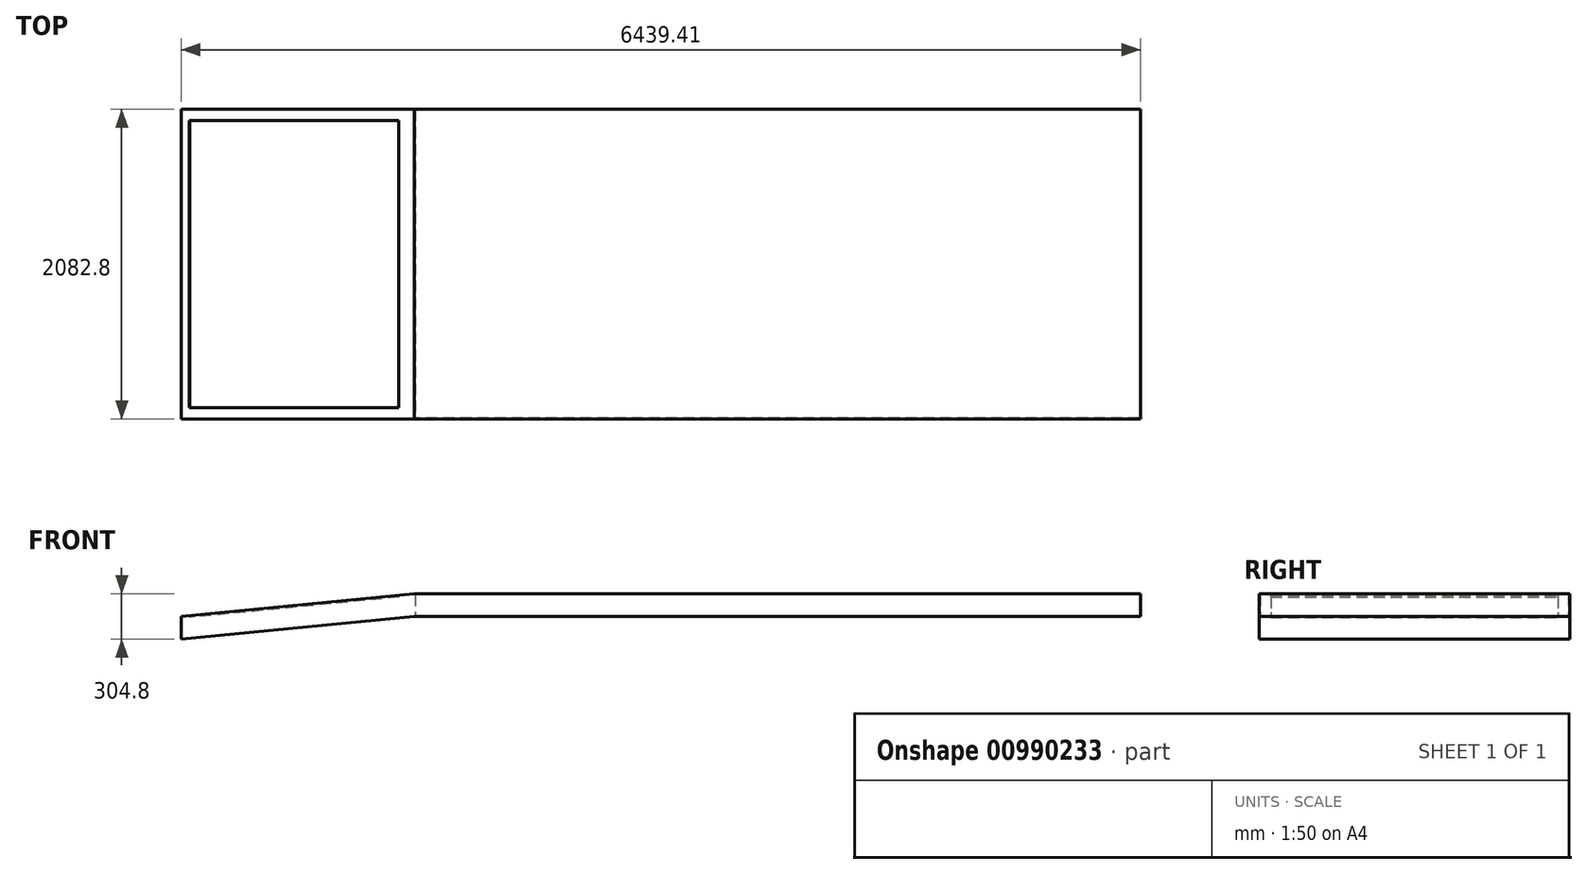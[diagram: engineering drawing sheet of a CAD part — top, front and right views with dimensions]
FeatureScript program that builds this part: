
annotation { "Feature Type Name" : "Feature", "Feature Type Description" : "" }
export const myFeature = defineFeature(function(context is Context, id is Id, definition is map)
    precondition{}
    {
        {
            var Q0;
            Q0=qCreatedBy(makeId("Top.planeOp"),FACE);
            var sketch = newSketch(context, id + "F0", { "sketchPlane" : qUnion([Q0])});
            skLineSegment(sketch, "E0.bottom", {"start": v(2438.4, 1041.4) * mm, "end": v(-2438.4, 1041.4) * mm});
            skLineSegment(sketch, "E0.top", {"start": v(2438.4, -1041.4) * mm, "end": v(-2438.4, -1041.4) * mm});
            skLineSegment(sketch, "E0.left", {"start": v(2438.4, 1041.4) * mm, "end": v(2438.4, -1041.4) * mm});
            skLineSegment(sketch, "E0.right", {"start": v(-2438.4, 1041.4) * mm, "end": v(-2438.4, -1041.4) * mm});
            skPoint(sketch, "E0.middle", {"position": v(0, 0) * mm});
            skSolve(sketch);
        }
        {
            var Q0;
            Q0 = qSketchRegion(id + "F0", true);
            extrude(context, id + "F1", {"entities" : qUnion([Q0]), "depth" : 152.4 * mm, "offsetDistance" : 25.4 * mm});
        }
        {
            var Q0;
            Q0=makeQuery(id+"F1.opExtrude","CAP_FACE",FACE,{"disambiguationData":[OSD([sQuery(id+"F0.wireOp",EDGE,"E0.bottom"),sQuery(id+"F0.wireOp",EDGE,"E0.top"),sQuery(id+"F0.wireOp",EDGE,"E0.left"),sQuery(id+"F0.wireOp",EDGE,"E0.right")])],"isStart":true});
            shell(context, id + "F2", {"entities" : qUnion([Q0]), "thickness" : 6.35 * mm});
        }
        {
            var Q0;
            Q0=qCreatedBy(makeId("Front.planeOp"),FACE);
            var sketch = newSketch(context, id + "F3", { "sketchPlane" : qUnion([Q0])});
            skLineSegment(sketch, "E1", {"start": v(-2438.4, 152.4) * mm, "end": v(-2438.4, 0) * mm});
            skLineSegment(sketch, "E2", {"start": v(-2438.4, 152.4) * mm, "end": v(-4001.01, 0) * mm});
            skLineSegment(sketch, "E3", {"start": v(-4001.01, 0) * mm, "end": v(-4001.01, -152.4) * mm});
            skLineSegment(sketch, "E4", {"start": v(-4001.01, -152.4) * mm, "end": v(-2438.4, 0) * mm});
            skSolve(sketch);
        }
        {
            var Q0;
            Q0 = qSketchRegion(id + "F3", true);
            extrude(context, id + "F4", {"entities" : qUnion([Q0]), "operationType" : NewBodyOperationType.ADD, "endBound" : BoundingType.SYMMETRIC, "depth" : 2082.8 * mm, "offsetDistance" : 25.4 * mm});
        }
        {
            var Q0;
            Q0=makeQuery(id+"F4.opExtrude","SWEPT_FACE",FACE,{"disambiguationData":[OSD([sQuery(id+"F3.wireOp",EDGE,"E2")])]});
            var sketch = newSketch(context, id + "F5", { "sketchPlane" : qUnion([Q0])});
            skLineSegment(sketch, "E5.bottom", {"start": v(-2516.92, -964.6) * mm, "end": v(-3928.25, -964.6) * mm});
            skLineSegment(sketch, "E5.top", {"start": v(-2516.92, 964.6) * mm, "end": v(-3928.25, 964.6) * mm});
            skLineSegment(sketch, "E5.left", {"start": v(-2516.92, -964.6) * mm, "end": v(-2516.92, 964.6) * mm});
            skLineSegment(sketch, "E5.right", {"start": v(-3928.25, -964.6) * mm, "end": v(-3928.25, 964.6) * mm});
            skPoint(sketch, "E5.middle", {"position": v(-3222.59, 0) * mm});
            skSolve(sketch);
        }
        {
            var Q0;
            Q0 = qSketchRegion(id + "F5", true);
            extrude(context, id + "F6", {"entities" : qUnion([Q0]), "operationType" : NewBodyOperationType.REMOVE, "oppositeDirection" : true, "depth" : 12.7 * mm, "offsetDistance" : 25.4 * mm});
        }
    });
